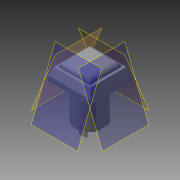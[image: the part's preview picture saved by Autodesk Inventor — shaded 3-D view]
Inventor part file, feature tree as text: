
AUTODESK INVENTOR PART (.ipt)
format: ipt  version: 2015 (Build 190159000, 159)  size: 209,920 bytes
history: native  units: in
note: dims shown in document units (in); Inventor stores cm internally (conversion verified against a paired STEP export)
features: extrude x10, sketch x10, plane x4, fillet x2
ambient origin geometry x8: Origin, YZ Plane, XZ Plane, XY Plane, X Axis, Y Axis, Z Axis, Center Point
bodies: Solid1 (feature_tree)
feature tree (26):
  extrude  "Extrusion1"  Depth=0.2165in
  extrude  "Extrusion2"  Depth=0.4961in
  extrude  "Extrusion3"  Depth=0.063in TaperAngle=0.0deg
  extrude  "Extrusion4"  Depth=0.685in
  plane  "Work Plane1"
  plane  "Work Plane2"
  plane  "Work Plane3"
  plane  "Work Plane4"
  extrude  "Extrusion5"  Depth=0.1063in
  extrude  "Extrusion6"  Depth=0.0787in
  extrude  "Extrusion7"  Depth=0.0472in
  extrude  "Extrusion8"  Depth=0.1181in TaperAngle=0.0deg
  fillet  "Fillet1"  Radius=0.1181in
  extrude  "Extrusion9"  Depth=0.1181in TaperAngle=0.0deg
  fillet  "Fillet2"  Radius=0.1181in
  extrude  "Extrusion10"  Depth=0.1575in
  sketch  "Sketch1"  dims[d0=0.4646in d1=0.2165in]
  sketch  "Sketch2"  dims[d2=0.4961in d3=0.0in d4=0.5276in]
  sketch  "Sketch3"  dims[d5=0.2362in d6=0.063in d7=0.0in]
  sketch  "Sketch4"  dims[d8=0.685in d9=0.685in]
  sketch  "Sketch5"  dims[d10=0.1063in d11=0.3425in]
  sketch  "Sketch6"  dims[d12=0.0787in d13=0.0in d14=0.5906in]
  sketch  "Sketch7"  dims[d15=0.5906in d16=0.0472in]
  sketch  "Sketch8"  dims[d17=0.0472in d18=0.1181in d19=0.0in d20=0.1181in d21=0.0in]
  sketch  "Sketch9"  dims[d22=0.1181in d23=0.0in d24=0.1181in d25=0.0in d26=0.1181in d27=0.0in]
  sketch  "Sketch10"  dims[d28=0.0197in d31=0.0394in d32=0.0394in d34=0.0394in d35=0.0394in d36=0.0787in d37=0.0in d38=0.0709in d39=0.1181in d40=0.0197in d41=0.1457in d42=0.1181in d43=0.1575in d44=0.0in]
